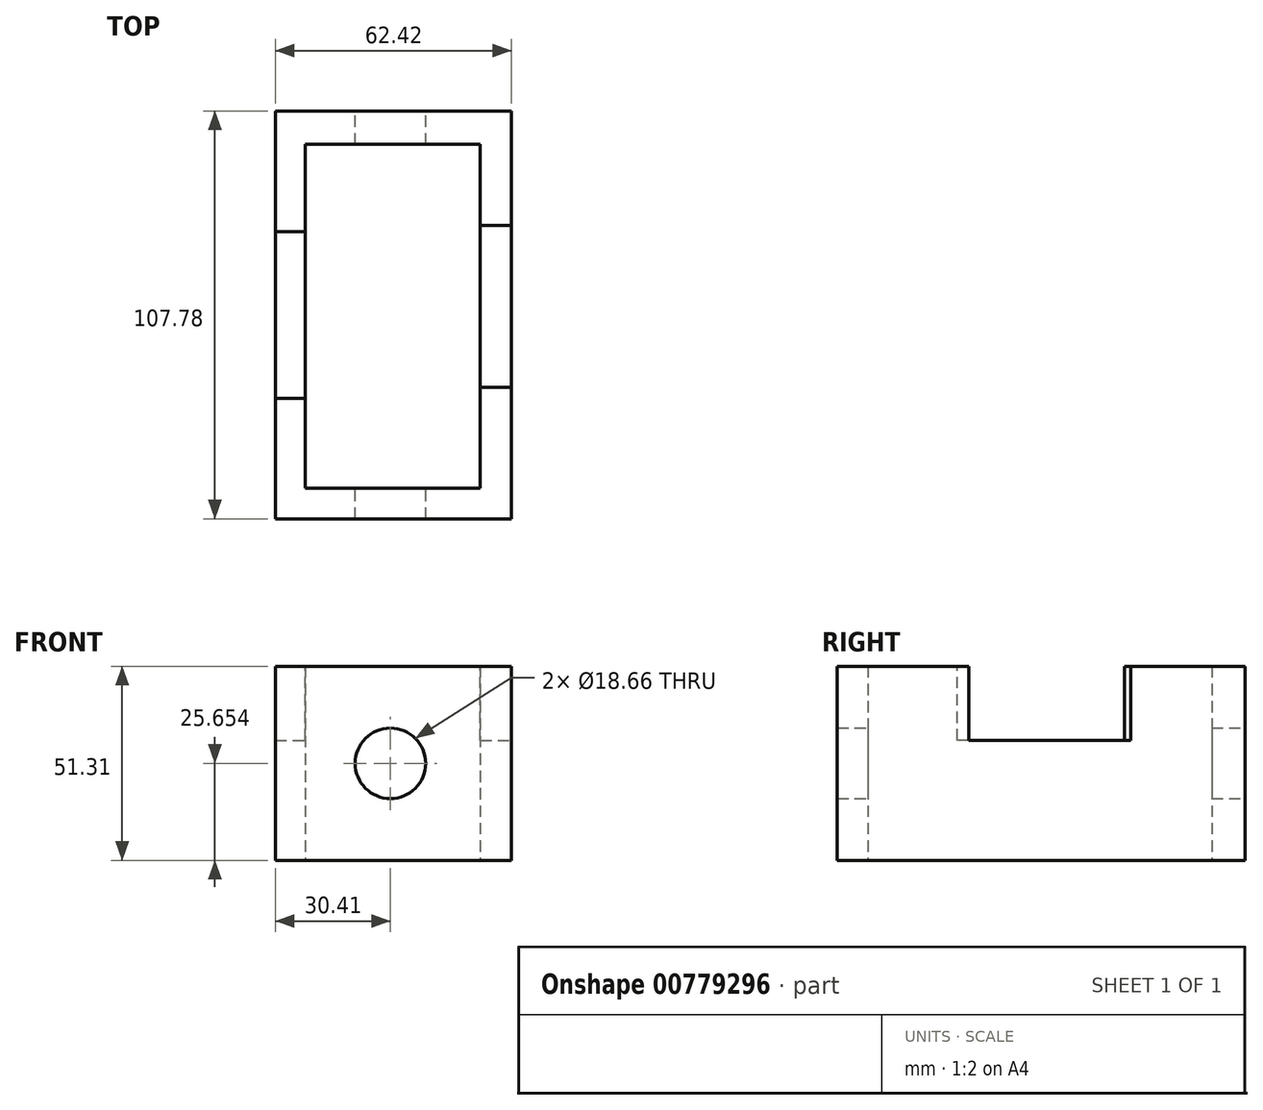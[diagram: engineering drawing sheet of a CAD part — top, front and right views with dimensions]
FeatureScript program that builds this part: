
annotation { "Feature Type Name" : "Feature", "Feature Type Description" : "" }
export const myFeature = defineFeature(function(context is Context, id is Id, definition is map)
    precondition{}
    {
        {
            var Q0;
            Q0=qCreatedBy(makeId("Top.planeOp"),FACE);
            var sketch = newSketch(context, id + "F0", { "sketchPlane" : qUnion([Q0])});
            skLineSegment(sketch, "E0.bottom", {"start": v(-62.42, 45.04) * mm, "end": v(0, 45.04) * mm});
            skLineSegment(sketch, "E0.top", {"start": v(-62.42, -62.74) * mm, "end": v(0, -62.74) * mm});
            skLineSegment(sketch, "E0.left", {"start": v(-62.42, 45.04) * mm, "end": v(-62.42, -62.74) * mm});
            skLineSegment(sketch, "E0.right", {"start": v(0, 45.04) * mm, "end": v(0, -62.74) * mm});
            skLineSegment(sketch, "E1.bottom", {"start": v(-54.52, 36.25) * mm, "end": v(-8.25, 36.25) * mm});
            skLineSegment(sketch, "E1.top", {"start": v(-54.52, -54.65) * mm, "end": v(-8.25, -54.65) * mm});
            skLineSegment(sketch, "E1.left", {"start": v(-54.52, 36.25) * mm, "end": v(-54.52, -54.65) * mm});
            skLineSegment(sketch, "E1.right", {"start": v(-8.25, 36.25) * mm, "end": v(-8.25, -54.65) * mm});
            skSolve(sketch);
        }
        {
            var Q0;
            Q0 = qSketchRegion(id + "F0", true);
            extrude(context, id + "F1", {"entities" : qUnion([Q0]), "depth" : 51.3 * mm, "offsetDistance" : 25.4 * mm});
        }
        {
            var Q0;
            Q0=makeQuery(id+"F1.opExtrude","CAP_FACE",FACE,{"disambiguationData":[OSD([sQuery(id+"F0.wireOp",EDGE,"E0.bottom"),sQuery(id+"F0.wireOp",EDGE,"E0.top"),sQuery(id+"F0.wireOp",EDGE,"E0.left"),sQuery(id+"F0.wireOp",EDGE,"E0.right"),sQuery(id+"F0.wireOp",EDGE,"E1.bottom"),sQuery(id+"F0.wireOp",EDGE,"E1.top"),sQuery(id+"F0.wireOp",EDGE,"E1.left"),sQuery(id+"F0.wireOp",EDGE,"E1.right")])],"isStart":false});
            var sketch = newSketch(context, id + "F2", { "sketchPlane" : qUnion([Q0])});
            skLineSegment(sketch, "E2.bottom", {"start": v(-8.25, -27.92) * mm, "end": v(0, -27.92) * mm});
            skLineSegment(sketch, "E2.top", {"start": v(-8.25, 14.87) * mm, "end": v(0, 14.87) * mm});
            skLineSegment(sketch, "E2.left", {"start": v(-8.25, -27.92) * mm, "end": v(-8.25, 14.87) * mm});
            skLineSegment(sketch, "E2.right", {"start": v(0, -27.92) * mm, "end": v(0, 14.87) * mm});
            skLineSegment(sketch, "E3.bottom", {"start": v(-62.42, -30.95) * mm, "end": v(-54.52, -30.95) * mm});
            skLineSegment(sketch, "E3.top", {"start": v(-62.42, 13.2) * mm, "end": v(-54.52, 13.2) * mm});
            skLineSegment(sketch, "E3.left", {"start": v(-62.42, -30.95) * mm, "end": v(-62.42, 13.2) * mm});
            skLineSegment(sketch, "E3.right", {"start": v(-54.52, -30.95) * mm, "end": v(-54.52, 13.2) * mm});
            skSolve(sketch);
        }
        {
            var Q0;
            Q0 = qSketchRegion(id + "F2", true);
            extrude(context, id + "F3", {"entities" : qUnion([Q0]), "operationType" : NewBodyOperationType.REMOVE, "oppositeDirection" : true, "depth" : 19.56 * mm, "offsetDistance" : 25.4 * mm});
        }
        {
            var Q0;
            Q0=makeQuery(id+"F1.opExtrude","SWEPT_FACE",FACE,{"disambiguationData":[OSD([sQuery(id+"F0.wireOp",EDGE,"E0.bottom")])]});
            var sketch = newSketch(context, id + "F4", { "sketchPlane" : qUnion([Q0])});
            skCircle(sketch, "E4", {"center": v(32.01, 25.65) * mm, "radius": 9.33 * mm});
            skPoint(sketch, "E4.centerSnap0", {"position": v(0, 25.65) * mm});
            skSolve(sketch);
        }
        {
            var Q0;
            Q0 = qSketchRegion(id + "F4", true);
            extrude(context, id + "F5", {"entities" : qUnion([Q0]), "operationType" : NewBodyOperationType.REMOVE, "oppositeDirection" : true, "depth" : 152.4 * mm, "offsetDistance" : 25.4 * mm});
        }
    });
